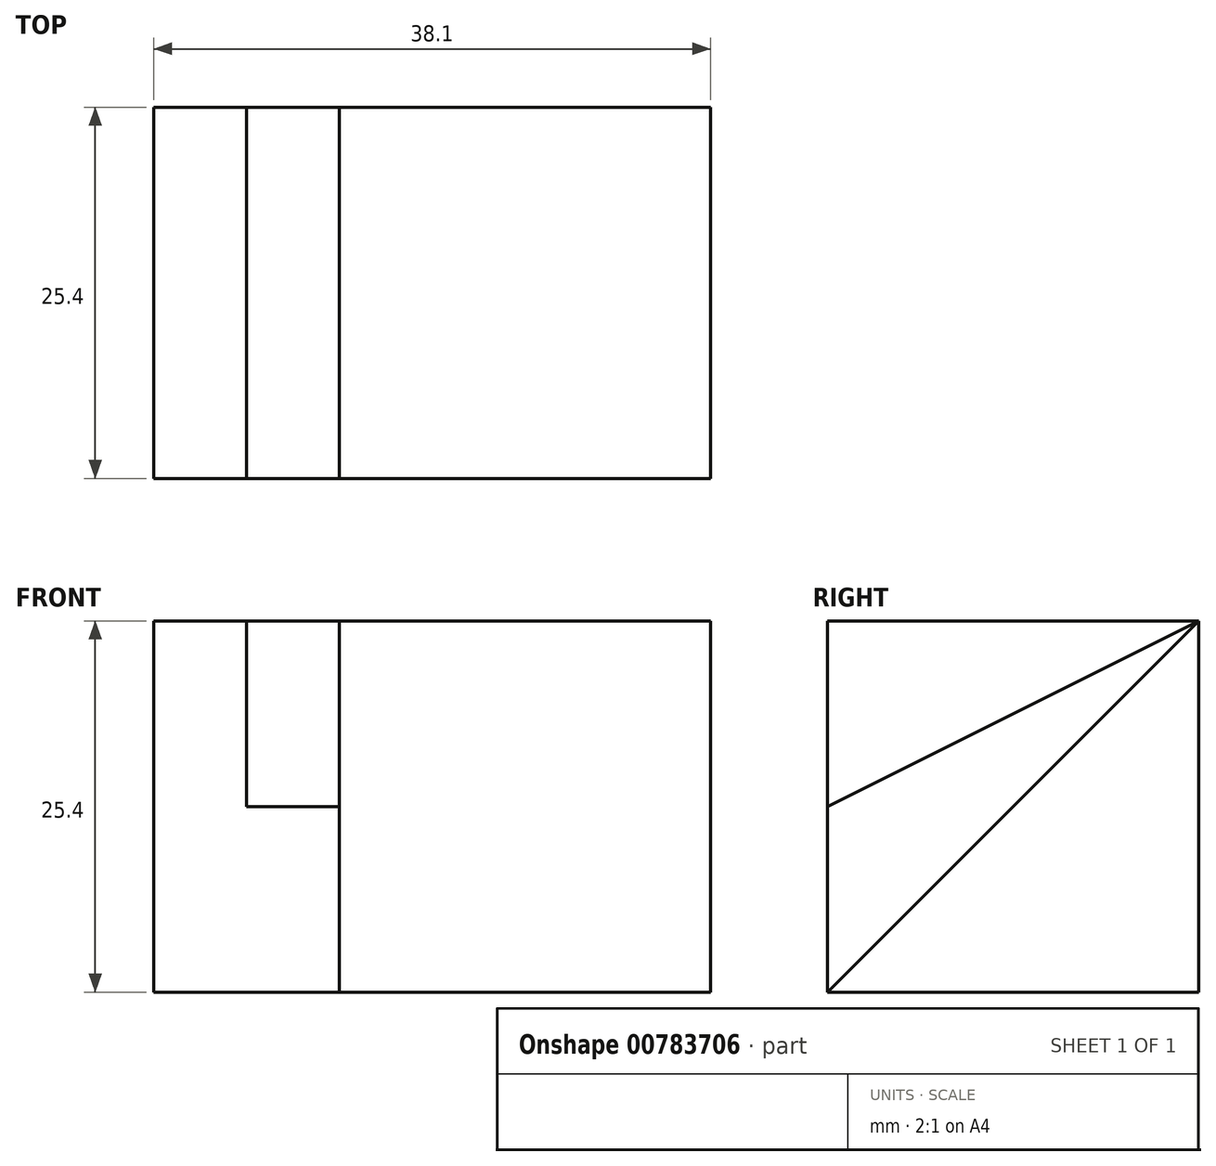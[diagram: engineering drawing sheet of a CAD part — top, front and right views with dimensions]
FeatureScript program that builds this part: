
annotation { "Feature Type Name" : "Feature", "Feature Type Description" : "" }
export const myFeature = defineFeature(function(context is Context, id is Id, definition is map)
    precondition{}
    {
        {
            var Q0;
            Q0=qCreatedBy(makeId("Right.planeOp"),FACE);
            var sketch = newSketch(context, id + "F0", { "sketchPlane" : qUnion([Q0])});
            skLineSegment(sketch, "E0", {"start": v(0, 0) * mm, "end": v(0, 25.4) * mm});
            skLineSegment(sketch, "E1", {"start": v(0, 25.4) * mm, "end": v(25.4, 25.4) * mm});
            skLineSegment(sketch, "E2", {"start": v(25.4, 25.4) * mm, "end": v(25.4, 0) * mm});
            skLineSegment(sketch, "E3", {"start": v(25.4, 0) * mm, "end": v(0, 0) * mm});
            skSolve(sketch);
        }
        {
            var Q0;
            Q0 = qSketchRegion(id + "F0", true);
            extrude(context, id + "F1", {"entities" : qUnion([Q0]), "depth" : 38.1 * mm, "offsetDistance" : 25.4 * mm});
        }
        {
            var Q0;
            Q0=makeQuery(id+"F1.opExtrude","CAP_FACE",FACE,{"disambiguationData":[OSD([sQuery(id+"F0.wireOp",EDGE,"E0"),sQuery(id+"F0.wireOp",EDGE,"E1"),sQuery(id+"F0.wireOp",EDGE,"E2"),sQuery(id+"F0.wireOp",EDGE,"E3")])],"isStart":false});
            var sketch = newSketch(context, id + "F2", { "sketchPlane" : qUnion([Q0])});
            skLineSegment(sketch, "E4", {"start": v(0, 0) * mm, "end": v(0, 12.7) * mm});
            skLineSegment(sketch, "E5", {"start": v(0, 0) * mm, "end": v(25.4, 0) * mm});
            skLineSegment(sketch, "E6", {"start": v(25.4, 0) * mm, "end": v(25.4, 25.4) * mm});
            skLineSegment(sketch, "E7", {"start": v(25.4, 25.4) * mm, "end": v(0, 12.7) * mm});
            skSolve(sketch);
        }
        {
            var Q0;
            {var subQ0=sQuery(id+"F2.wireOp",EDGE,"E7");Q0=makeQuery(id+"F2.imprint","IMPRINT",FACE,{"disambiguationData":[TD([[makeQuery(id+"F2.imprint","IMPRINT",EDGE,{"derivedFrom":subQ0}),-1.0]])]});}
            extrude(context, id + "F3", {"entities" : qUnion([Q0]), "operationType" : NewBodyOperationType.REMOVE, "oppositeDirection" : true, "depth" : 31.75 * mm, "offsetDistance" : 25.4 * mm});
        }
        {
            var Q0;
            Q0=makeQuery(id+"F1.opExtrude","CAP_FACE",FACE,{"disambiguationData":[OSD([sQuery(id+"F0.wireOp",EDGE,"E0"),sQuery(id+"F0.wireOp",EDGE,"E1"),sQuery(id+"F0.wireOp",EDGE,"E2"),sQuery(id+"F0.wireOp",EDGE,"E3")])],"isStart":false});
            var sketch = newSketch(context, id + "F4", { "sketchPlane" : qUnion([Q0])});
            skLineSegment(sketch, "E8", {"start": v(0, 0) * mm, "end": v(25.4, 25.4) * mm});
            skLineSegment(sketch, "E9", {"start": v(25.4, 25.4) * mm, "end": v(25.4, 0) * mm});
            skLineSegment(sketch, "E10", {"start": v(25.4, 0) * mm, "end": v(0, 0) * mm});
            skSolve(sketch);
        }
        {
            var Q0;
            Q0=makeQuery(id+"F4.imprint","IMPRINT",FACE,{"disambiguationData":[TD([[makeQuery(id+"F4.imprint","IMPRINT",EDGE,{"derivedFrom":sQuery(id+"F4.wireOp",EDGE,"E8")}),1.0]])]});
            extrude(context, id + "F5", {"entities" : qUnion([Q0]), "operationType" : NewBodyOperationType.REMOVE, "oppositeDirection" : true, "depth" : 25.4 * mm, "offsetDistance" : 25.4 * mm});
        }
    });
